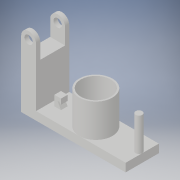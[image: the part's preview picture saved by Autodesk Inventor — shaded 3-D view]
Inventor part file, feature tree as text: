
AUTODESK INVENTOR PART (.ipt)
format: ipt  version: 2019 (Build 230136000, 136)  size: 176,128 bytes
history: native  units: in
note: dims shown in document units (in); Inventor stores cm internally (conversion verified against a paired STEP export)
features: sketch x8, extrude x6
ambient origin geometry x8: Origin, YZ Plane, XZ Plane, XY Plane, X Axis, Y Axis, Z Axis, Center Point
bodies: Solid1 (feature_tree)
feature tree (14):
  extrude  "Extrusion1"  Depth=0.1969in
  sketch  "Sketch2"  dims[d6=0.1772in d7=0.1969in]
  sketch  "Sketch6"  dims[d8=0.3543in d9=2.126in]
  extrude  "Extrusion5"  Depth=0.1969in
  sketch  "Sketch8"  dims[d13=0.2559in d14=0.7874in]
  extrude  "Extrusion6"  Depth=2.126in
  extrude  "Extrusion7"  Depth=0.1181in
  extrude  "Extrusion8"  Depth=0.7874in
  extrude  "Extrusion9"  Depth=0.3937in
  sketch  "Sketch1"  dims[d0=1.5748in d2=0.1969in]
  sketch  "Sketch7"  dims[d10=0.7874in d11=0.0in d12=0.1181in]
  sketch  "Sketch9"  dims[d16=1.0236in d19=0.3937in]
  sketch  "Sketch10"  dims[d20=0.1575in]
  sketch  "Sketch11"  dims[d21=0.3937in d22=0.5512in d40=0.5512in d41=0.5512in d42=0.5906in d43=0.5512in d44=0.0in d47=1.2795in d48=0.7874in d49=0.0in d50=0.7087in d51=0.9843in d52=0.0in d53=0.1575in d54=0.1575in d55=0.315in d56=0.1181in d57=0.2362in d58=0.0in d59=0.0787in d60=0.0394in d61=0.1496in d62=0.1102in d63=0.1575in d64=0.0in]
